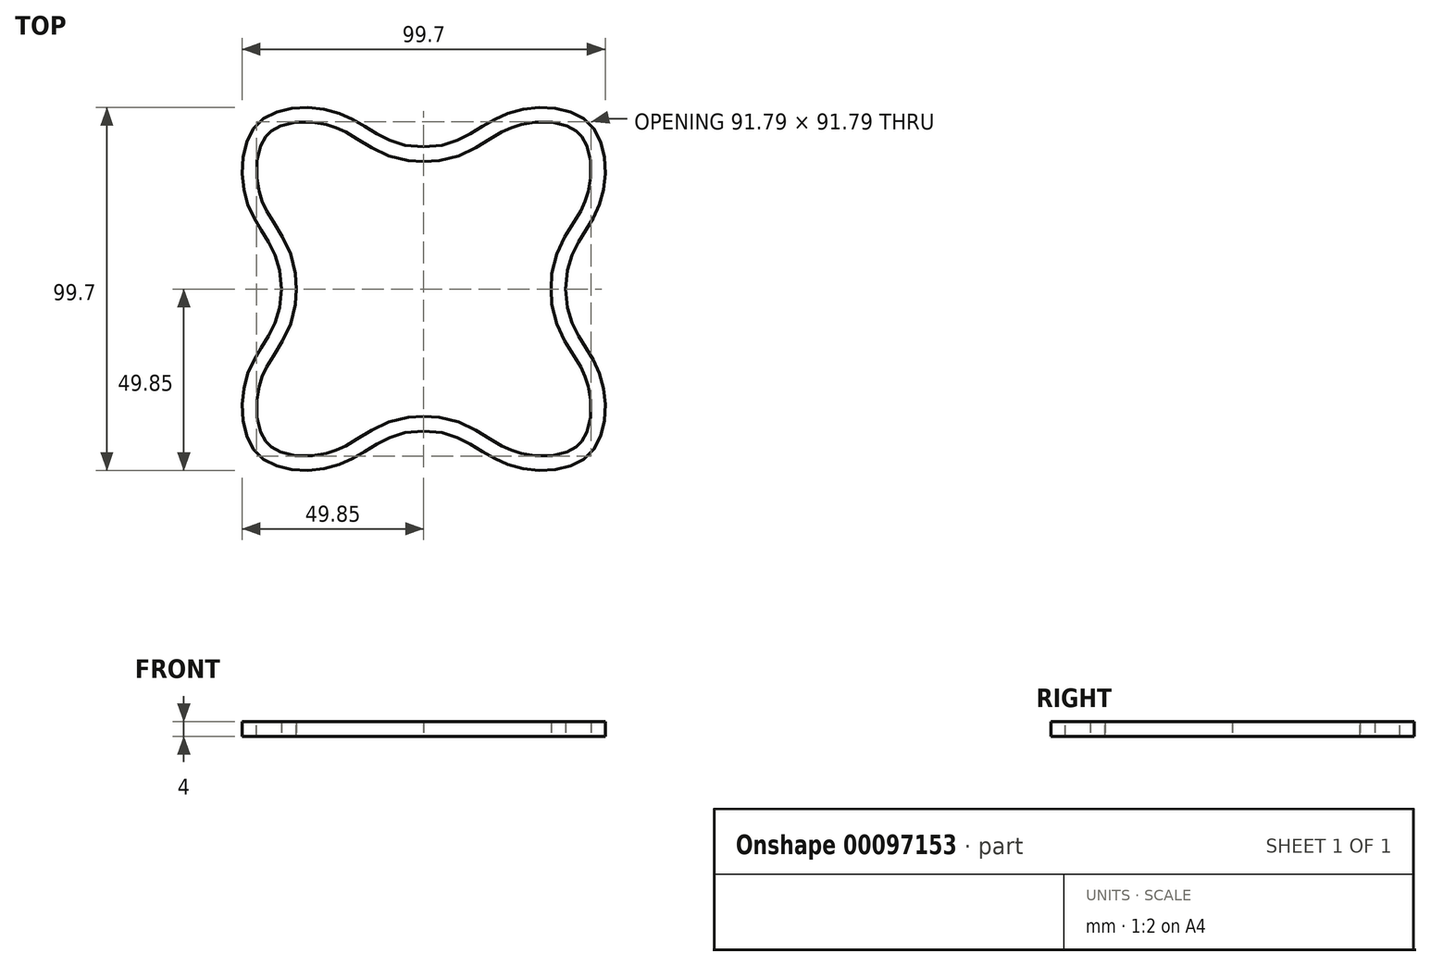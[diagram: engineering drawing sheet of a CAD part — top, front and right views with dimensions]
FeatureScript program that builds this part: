
annotation { "Feature Type Name" : "Feature", "Feature Type Description" : "" }
export const myFeature = defineFeature(function(context is Context, id is Id, definition is map)
    precondition{}
    {
        {
            var Q0;
            Q0=qCreatedBy(makeId("Top.planeOp"),FACE);
            var sketch = newSketch(context, id + "F0", { "sketchPlane" : qUnion([Q0])});
            skPoint(sketch, "E0.middle", {"position": v(0, 0) * mm});
            skLineSegment(sketch, "E1", {"start": v(-49, 49) * mm, "end": v(49, -49) * mm, "construction": true});
            skFitSpline(sketch, "E2", {"points": [v(0, 39) * mm, v(-22.37, 47.95) * mm, v(-45.46, 45.46) * mm, v(-47.95, 22.37) * mm, v(-39, 0) * mm], "startDerivative": vector(-130.17, 0) * mm, "endDerivative": vector(0, -130.17) * mm});
            skLineSegment(sketch, "E3", {"start": v(0, 0) * mm, "end": v(-49, 0) * mm, "construction": true});
            skLineSegment(sketch, "E4", {"start": v(0, 0) * mm, "end": v(0, 49) * mm, "construction": true});
            skLineSegment(sketch, "E5", {"start": v(-22.37, 47.95) * mm, "end": v(-47.95, 22.37) * mm, "construction": true});
            skLineSegment(sketch, "E6", {"start": v(0, 0) * mm, "end": v(-35.16, 35.16) * mm, "construction": true});
            skFitSpline(sketch, "E7.MirrorCS", {"points": [v(0, 39) * mm, v(22.37, 47.95) * mm, v(45.46, 45.46) * mm, v(47.95, 22.37) * mm, v(39, 0) * mm], "startDerivative": vector(130.17, 0) * mm, "endDerivative": vector(0, -130.17) * mm});
            skLineSegment(sketch, "E8", {"start": v(0, 39) * mm, "end": v(-10.95, 39) * mm, "construction": true});
            skLineSegment(sketch, "E9", {"start": v(-39, 0) * mm, "end": v(-39, 10.95) * mm, "construction": true});
            skFitSpline(sketch, "E10.MirrorCS", {"points": [v(0, -39) * mm, v(22.37, -47.95) * mm, v(45.46, -45.46) * mm, v(47.95, -22.37) * mm, v(39, 0) * mm], "startDerivative": vector(130.17, 0) * mm, "endDerivative": vector(0, 130.17) * mm});
            skFitSpline(sketch, "E11.MirrorCS", {"points": [v(0, -39) * mm, v(-22.37, -47.95) * mm, v(-45.46, -45.46) * mm, v(-47.95, -22.37) * mm, v(-39, 0) * mm], "startDerivative": vector(-130.17, 0) * mm, "endDerivative": vector(0, 130.17) * mm});
            skFitSpline(sketch, "E12.0", {"points": [v(0, 35) * mm, v(-1.54, 35) * mm, v(-4.42, 35.2) * mm, v(-8.24, 36.07) * mm, v(-11.56, 37.33) * mm, v(-14.45, 38.83) * mm, v(-16.98, 40.38) * mm, v(-18.9, 41.61) * mm, v(-20.38, 42.5) * mm, v(-21.47, 43.13) * mm, v(-22.56, 43.68) * mm, v(-23.49, 44.1) * mm, v(-24.25, 44.4) * mm, v(-25.04, 44.67) * mm, v(-26.08, 45) * mm, v(-27.4, 45.3) * mm, v(-29.2, 45.64) * mm, v(-31.51, 45.88) * mm, v(-34.28, 45.85) * mm, v(-36.9, 45.5) * mm, v(-38.84, 44.93) * mm, v(-40.21, 44.34) * mm, v(-41.14, 43.84) * mm, v(-41.81, 43.36) * mm, v(-42.3, 42.96) * mm, v(-42.64, 42.64) * mm, v(-42.96, 42.3) * mm, v(-43.36, 41.81) * mm, v(-43.84, 41.14) * mm, v(-44.34, 40.21) * mm, v(-44.93, 38.84) * mm, v(-45.5, 36.9) * mm, v(-45.85, 34.28) * mm, v(-45.88, 31.51) * mm, v(-45.64, 29.2) * mm, v(-45.3, 27.4) * mm, v(-45, 26.08) * mm, v(-44.67, 25.04) * mm, v(-44.4, 24.25) * mm, v(-44.1, 23.49) * mm, v(-43.68, 22.56) * mm, v(-43.13, 21.47) * mm, v(-42.5, 20.38) * mm, v(-41.61, 18.9) * mm, v(-40.38, 16.98) * mm, v(-38.83, 14.45) * mm, v(-37.33, 11.56) * mm, v(-36.07, 8.24) * mm, v(-35.2, 4.42) * mm, v(-35, 1.54) * mm, v(-35, 0) * mm]});
            skFitSpline(sketch, "E12.1", {"points": [v(0, 35) * mm, v(1.54, 35) * mm, v(4.42, 35.2) * mm, v(8.24, 36.07) * mm, v(11.56, 37.33) * mm, v(14.45, 38.83) * mm, v(16.98, 40.38) * mm, v(18.9, 41.61) * mm, v(20.38, 42.5) * mm, v(21.47, 43.13) * mm, v(22.56, 43.68) * mm, v(23.49, 44.1) * mm, v(24.25, 44.4) * mm, v(25.04, 44.67) * mm, v(26.08, 45) * mm, v(27.4, 45.3) * mm, v(29.2, 45.64) * mm, v(31.51, 45.88) * mm, v(34.28, 45.85) * mm, v(36.9, 45.5) * mm, v(38.84, 44.93) * mm, v(40.21, 44.34) * mm, v(41.14, 43.84) * mm, v(41.81, 43.36) * mm, v(42.3, 42.96) * mm, v(42.64, 42.64) * mm, v(42.96, 42.3) * mm, v(43.36, 41.81) * mm, v(43.84, 41.14) * mm, v(44.34, 40.21) * mm, v(44.93, 38.84) * mm, v(45.5, 36.9) * mm, v(45.85, 34.28) * mm, v(45.88, 31.51) * mm, v(45.64, 29.2) * mm, v(45.3, 27.4) * mm, v(45, 26.08) * mm, v(44.67, 25.04) * mm, v(44.4, 24.25) * mm, v(44.1, 23.49) * mm, v(43.68, 22.56) * mm, v(43.13, 21.47) * mm, v(42.5, 20.38) * mm, v(41.61, 18.9) * mm, v(40.38, 16.98) * mm, v(38.83, 14.45) * mm, v(37.33, 11.56) * mm, v(36.07, 8.24) * mm, v(35.2, 4.42) * mm, v(35, 1.54) * mm, v(35, 0) * mm]});
            skFitSpline(sketch, "E12.2", {"points": [v(0, -35) * mm, v(1.54, -35) * mm, v(4.42, -35.2) * mm, v(8.24, -36.07) * mm, v(11.56, -37.33) * mm, v(14.45, -38.83) * mm, v(16.98, -40.38) * mm, v(18.9, -41.61) * mm, v(20.38, -42.5) * mm, v(21.47, -43.13) * mm, v(22.56, -43.68) * mm, v(23.49, -44.1) * mm, v(24.25, -44.4) * mm, v(25.04, -44.67) * mm, v(26.08, -45) * mm, v(27.4, -45.3) * mm, v(29.2, -45.64) * mm, v(31.51, -45.88) * mm, v(34.28, -45.85) * mm, v(36.9, -45.5) * mm, v(38.84, -44.93) * mm, v(40.21, -44.34) * mm, v(41.14, -43.84) * mm, v(41.81, -43.36) * mm, v(42.3, -42.96) * mm, v(42.64, -42.64) * mm, v(42.96, -42.3) * mm, v(43.36, -41.81) * mm, v(43.84, -41.14) * mm, v(44.34, -40.21) * mm, v(44.93, -38.84) * mm, v(45.5, -36.9) * mm, v(45.85, -34.28) * mm, v(45.88, -31.51) * mm, v(45.64, -29.2) * mm, v(45.3, -27.4) * mm, v(45, -26.08) * mm, v(44.67, -25.04) * mm, v(44.4, -24.25) * mm, v(44.1, -23.49) * mm, v(43.68, -22.56) * mm, v(43.13, -21.47) * mm, v(42.5, -20.38) * mm, v(41.61, -18.9) * mm, v(40.38, -16.98) * mm, v(38.83, -14.45) * mm, v(37.33, -11.56) * mm, v(36.07, -8.24) * mm, v(35.2, -4.42) * mm, v(35, -1.54) * mm, v(35, 0) * mm]});
            skFitSpline(sketch, "E12.3", {"points": [v(0, -35) * mm, v(-1.54, -35) * mm, v(-4.42, -35.2) * mm, v(-8.24, -36.07) * mm, v(-11.56, -37.33) * mm, v(-14.45, -38.83) * mm, v(-16.98, -40.38) * mm, v(-18.9, -41.61) * mm, v(-20.38, -42.5) * mm, v(-21.47, -43.13) * mm, v(-22.56, -43.68) * mm, v(-23.49, -44.1) * mm, v(-24.25, -44.4) * mm, v(-25.04, -44.67) * mm, v(-26.08, -45) * mm, v(-27.4, -45.3) * mm, v(-29.2, -45.64) * mm, v(-31.51, -45.88) * mm, v(-34.28, -45.85) * mm, v(-36.9, -45.5) * mm, v(-38.84, -44.93) * mm, v(-40.21, -44.34) * mm, v(-41.14, -43.84) * mm, v(-41.81, -43.36) * mm, v(-42.3, -42.96) * mm, v(-42.64, -42.64) * mm, v(-42.96, -42.3) * mm, v(-43.36, -41.81) * mm, v(-43.84, -41.14) * mm, v(-44.34, -40.21) * mm, v(-44.93, -38.84) * mm, v(-45.5, -36.9) * mm, v(-45.85, -34.28) * mm, v(-45.88, -31.51) * mm, v(-45.64, -29.2) * mm, v(-45.3, -27.4) * mm, v(-45, -26.08) * mm, v(-44.67, -25.04) * mm, v(-44.4, -24.25) * mm, v(-44.1, -23.49) * mm, v(-43.68, -22.56) * mm, v(-43.13, -21.47) * mm, v(-42.5, -20.38) * mm, v(-41.61, -18.9) * mm, v(-40.38, -16.98) * mm, v(-38.83, -14.45) * mm, v(-37.33, -11.56) * mm, v(-36.07, -8.24) * mm, v(-35.2, -4.42) * mm, v(-35, -1.54) * mm, v(-35, 0) * mm]});
            skSolve(sketch);
        }
        {
            var Q0;
            Q0=makeQuery(id+"F0.imprint","IMPRINT",FACE,{"disambiguationData":[TD([[makeQuery(id+"F0.imprint","IMPRINT",EDGE,{"derivedFrom":sQuery(id+"F0.wireOp",EDGE,"E2")}),1.0]])]});
            extrude(context, id + "F1", {"entities" : qUnion([Q0]), "depth" : 4 * mm});
        }
    });
